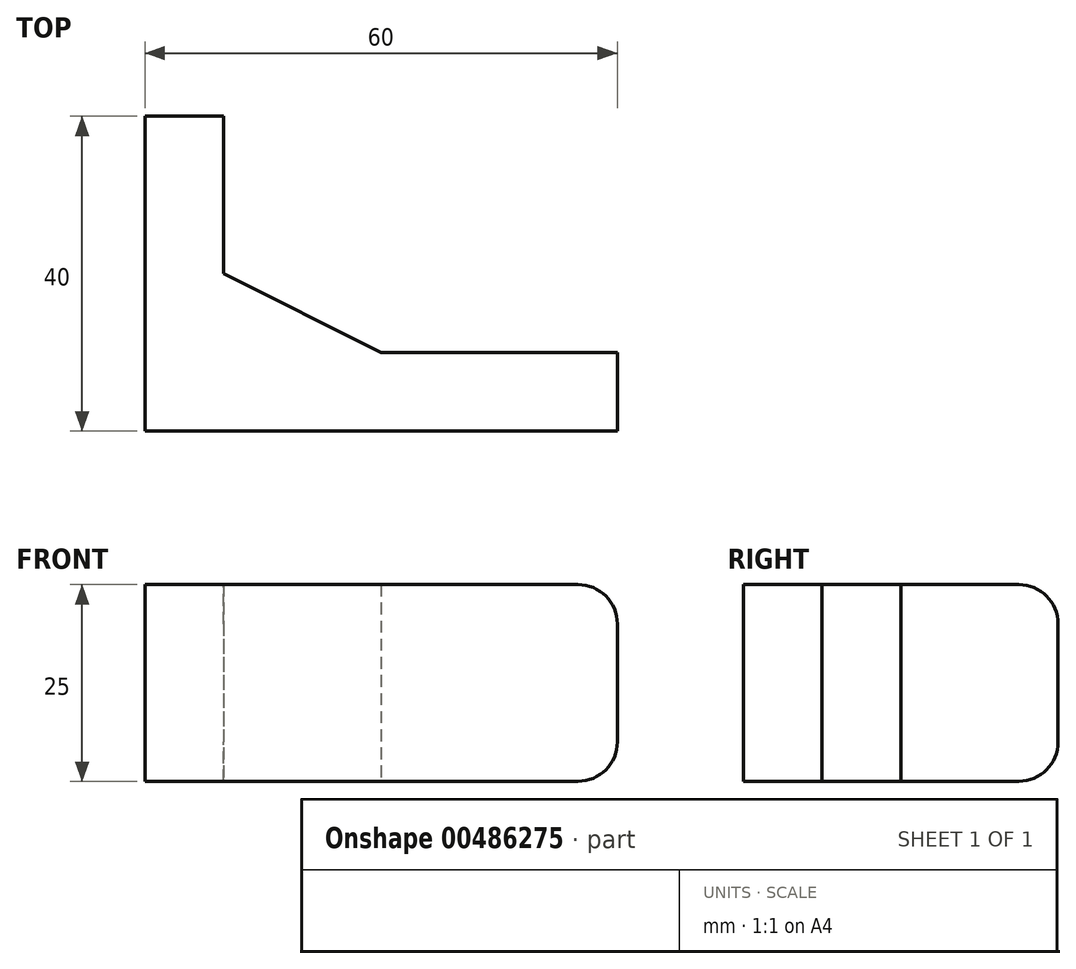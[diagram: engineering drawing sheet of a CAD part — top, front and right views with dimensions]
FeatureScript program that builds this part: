
annotation { "Feature Type Name" : "Feature", "Feature Type Description" : "" }
export const myFeature = defineFeature(function(context is Context, id is Id, definition is map)
    precondition{}
    {
        {
            var Q0;
            Q0=qCreatedBy(makeId("Top.planeOp"),FACE);
            var sketch = newSketch(context, id + "F0", { "sketchPlane" : qUnion([Q0])});
            skLineSegment(sketch, "E0", {"start": v(-34.2, 26.66) * mm, "end": v(-34.2, -13.34) * mm});
            skLineSegment(sketch, "E1", {"start": v(-34.2, 26.66) * mm, "end": v(-24.2, 26.66) * mm});
            skLineSegment(sketch, "E2", {"start": v(-34.2, -13.34) * mm, "end": v(25.8, -13.34) * mm});
            skLineSegment(sketch, "E3", {"start": v(25.8, -13.34) * mm, "end": v(25.8, -3.34) * mm});
            skLineSegment(sketch, "E4", {"start": v(25.8, -3.34) * mm, "end": v(-4.2, -3.34) * mm});
            skLineSegment(sketch, "E5", {"start": v(-24.2, 26.66) * mm, "end": v(-24.2, 6.66) * mm});
            skLineSegment(sketch, "E6", {"start": v(-24.2, 6.66) * mm, "end": v(-4.2, -3.34) * mm});
            skSolve(sketch);
        }
        {
            var Q0;
            Q0=makeQuery(id+"F0.imprint","IMPRINT",FACE,{"disambiguationData":[TD([[makeQuery(id+"F0.imprint","IMPRINT",EDGE,{"derivedFrom":sQuery(id+"F0.wireOp",EDGE,"E0")}),1.0]])]});
            extrude(context, id + "F1", {"entities" : qUnion([Q0]), "depth" : 25 * mm});
        }
        {
            var Q0;
            Q0=makeQuery(id+"F1.opExtrude","CAP_EDGE",EDGE,{"disambiguationData":[OSD([sQuery(id+"F0.wireOp",EDGE,"E1")])],"isStart":false});
            var Q1;
            Q1=makeQuery(id+"F1.opExtrude","CAP_EDGE",EDGE,{"disambiguationData":[OSD([sQuery(id+"F0.wireOp",EDGE,"E1")])],"isStart":true});
            fillet(context, id + "F2", {"entities" : qUnion([Q0, Q1]), "radius" : 5 * mm, "tangentPropagation" : true, "allowEdgeOverflow" : false});
        }
        {
            var Q0;
            Q0=makeQuery(id+"F1.opExtrude","CAP_EDGE",EDGE,{"disambiguationData":[OSD([sQuery(id+"F0.wireOp",EDGE,"E3")])],"isStart":false});
            var Q1;
            Q1=makeQuery(id+"F1.opExtrude","CAP_EDGE",EDGE,{"disambiguationData":[OSD([sQuery(id+"F0.wireOp",EDGE,"E3")])],"isStart":true});
            fillet(context, id + "F3", {"entities" : qUnion([Q0, Q1]), "radius" : 5 * mm, "tangentPropagation" : true, "allowEdgeOverflow" : false});
        }
    });
